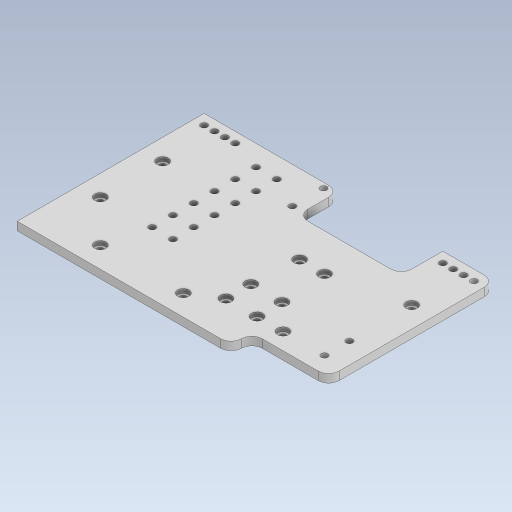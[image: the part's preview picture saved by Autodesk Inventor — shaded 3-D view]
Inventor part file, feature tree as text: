
AUTODESK INVENTOR PART (.ipt)
format: ipt  version: 2023.5 (Build 275446000, 446)  size: 234,496 bytes
history: native  units: mm
features: extrude x2, sketch x1, fillet x1
ambient origin geometry x8: Origin, YZ Plane, XZ Plane, XY Plane, X Axis, Y Axis, Z Axis, Center Point
bodies: Solid1 (feature_tree)
feature tree (4):
  sketch  "Sketch1"  dims[d8=4.0mm d9=0.0mm d10=2.0mm d11=0.0mm d12=140.0mm d13=90.0mm d14=10.0mm d15=10.0mm d16=10.0mm d17=10.0mm d18=10.0mm d19=10.0mm d20=10.0mm d21=3.2mm d22=2.5mm d23=5.0mm d24=3.2mm d25=15.0mm d26=3.2mm d27=3.2mm d28=10.0mm d29=3.2mm d30=10.0mm d31=3.2mm d32=10.0mm d33=10.0mm d35=5.0mm d36=25.0mm d37=3.3mm d38=5.0mm d39=5.0mm d40=3.2mm d41=5.5mm d42=3.2mm d43=3.2mm d44=5.5mm d45=5.5mm d46=10.0mm]
  extrude  "Extrusion1"  Depth=2.0mm TaperAngle=0.0deg
  extrude  "Extrusion2"  Depth=140.0mm
  fillet  "Fillet1"  Radius=90.0mm
